# Revit family: Reece_Shower_Kado_Lux_Walk In Shower Screen_Curved
name_source: partatom
category: Plumbing Fixtures
revit_build: Autodesk Revit 2018 (Build: 20190510_1515(x64)
units: mm (PartAtom-declared; Revit-internal decimal feet)

## family parameters
Always vertical = Yes
Cut with Voids When Loaded = Yes
Part Type = Normal
Room Calculation Point = Yes
Round Connector Dimension = Use Diameter
Shared = Yes
Work Plane-Based = Yes

## types (1)
- 1000 mm_With Wall Support_Chrome
    Default Elevation = 0 mm  [stored 0 ft]
    Description = Kado Lux Walk In Curved Shower Screen 1200 Chrome
    Disclaimer = THIS FILE IS THE PROPERTY OF THE REECE GROUP. IT MAY NOT BE REPRODUCED, REVERSE-ENGINEERED OR MODIFIED. ANY REPUBLICATION, TRANSMISSION OR DISTRIBUTION FOR THE PURPOSE OF COMMERCIALLY EXPLOITING THE FILES IS PROHIBITED.
    Keynote = Product #9507353, Reece_Shower_Kado_Lux_Walk In Shower Screen_Curved - 1000 mm_With Wall Support_Chrome
    Manufacturer = Kado
    Model = Lux
    Reece_Detail_Additional = Walk In Shower Screen
    Reece_Detail_Disclaimer = THIS FILE IS THE PROPERTY OF THE REECE GROUP. IT MAY NOT BE REPRODUCED, REVERSE-ENGINEERED OR MODIFIED. ANY REPUBLICATION, TRANSMISSION OR DISTRIBUTION FOR THE PURPOSE OF COMMERCIALLY EXPLOITING THE FILES IS PROHIBITED.
    Reece_Detail_Function = Curved
    Reece_Material_Main = Reece_Brass_Chrome
    Reece_Material_Screen = Reece_Safety Glass_Transparent
    Reece_Overall_Depth = 900 mm  [stored 2.95276 ft]
    Reece_Overall_Height = 2020 mm  [stored 6.6273 ft]
    Reece_Product_Brand = Kado
    Reece_Product_Description = Kado Lux Walk In Curved Shower Screen 1200 Chrome
    Reece_Product_Mount = Wall Mounted
    Reece_Product_Number = 9507353
    Reece_Product_Sub Brand = Lux
    Reece_Product_Type = Shower
    Reece_Product_Web Page = https://www.reece.com.au
    Reece_Screen_Height = 2000 mm  [stored 6.56168 ft]
    Reece_Screen_Size = 1200 mm
    Type Comments = Shower
    URL = https://www.reece.com.au

note: [stored X ft] marks values corroborated as IEEE doubles in the binary element streams (Revit-internal decimal feet)

## geometry (parser evidence)
native form markers: Sweep x2
no freeform markers — native parametric forms only
